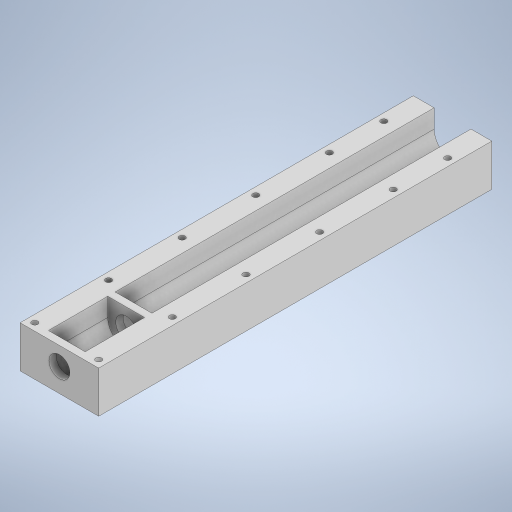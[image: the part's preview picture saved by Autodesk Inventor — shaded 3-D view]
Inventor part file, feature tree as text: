
AUTODESK INVENTOR PART (.ipt)
format: ipt  version: 2023 (Build 270158000, 158)  size: 316,416 bytes
history: native  units: mm
features: sketch x6, extrude x4, hole x2, projected_geometry x1
ambient origin geometry x8: Origin, YZ Plane, XZ Plane, XY Plane, X Axis, Y Axis, Z Axis, Center Point
bodies: Solid1 (feature_tree)
feature tree (13):
  extrude  "Extrusion1"  Depth=24.2mm TaperAngle=0.0deg
  extrude  "Extrusion3"  Depth=32.0mm
  extrude  "Extrusion4"  Depth=3.0mm TaperAngle=0.0deg
  extrude  "Extrusion5"  Depth=130.0mm TaperAngle=0.0deg
  hole  "Hole1"  [1 undecoded]
  hole  "Hole3"  [1 undecoded]
  sketch  "Sketch1"  dims[d0=15.0mm d3=24.2mm d4=0.0mm]
  sketch  "Sketch2"  dims[d5=32.0mm d6=2.0mm]
  projected_geometry  "Projected Loop1"
  sketch  "Sketch4"  dims[d10=8.5mm d11=3.0mm d12=0.0mm]
  sketch  "Sketch5"  dims[d13=3.0mm d14=0.0mm d15=130.0mm d16=0.0mm]
  sketch  "Sketch6"  dims[d17=3.0mm d18=3.0mm]
  sketch  "Sketch7"  dims[d19=2.38125mm d20=6.0mm d21=4.0mm d22=2.0mm d23=90.0deg d24=10.0mm d25=20.594885mm d27=3.0mm d42=50.0mm d44=30.0mm d45=10.0mm d47=10.0mm d49=3.0mm d50=15.0mm d51=2.38125mm d52=6.0mm d53=4.0mm d54=2.0mm d55=90.0deg d56=10.0mm d57=20.594885mm]
note: 2 required parameter values undecoded (feature->parameter linkage not recoverable at this tier; creation-order binding heuristic only, values carry confidence <= 0.55)
